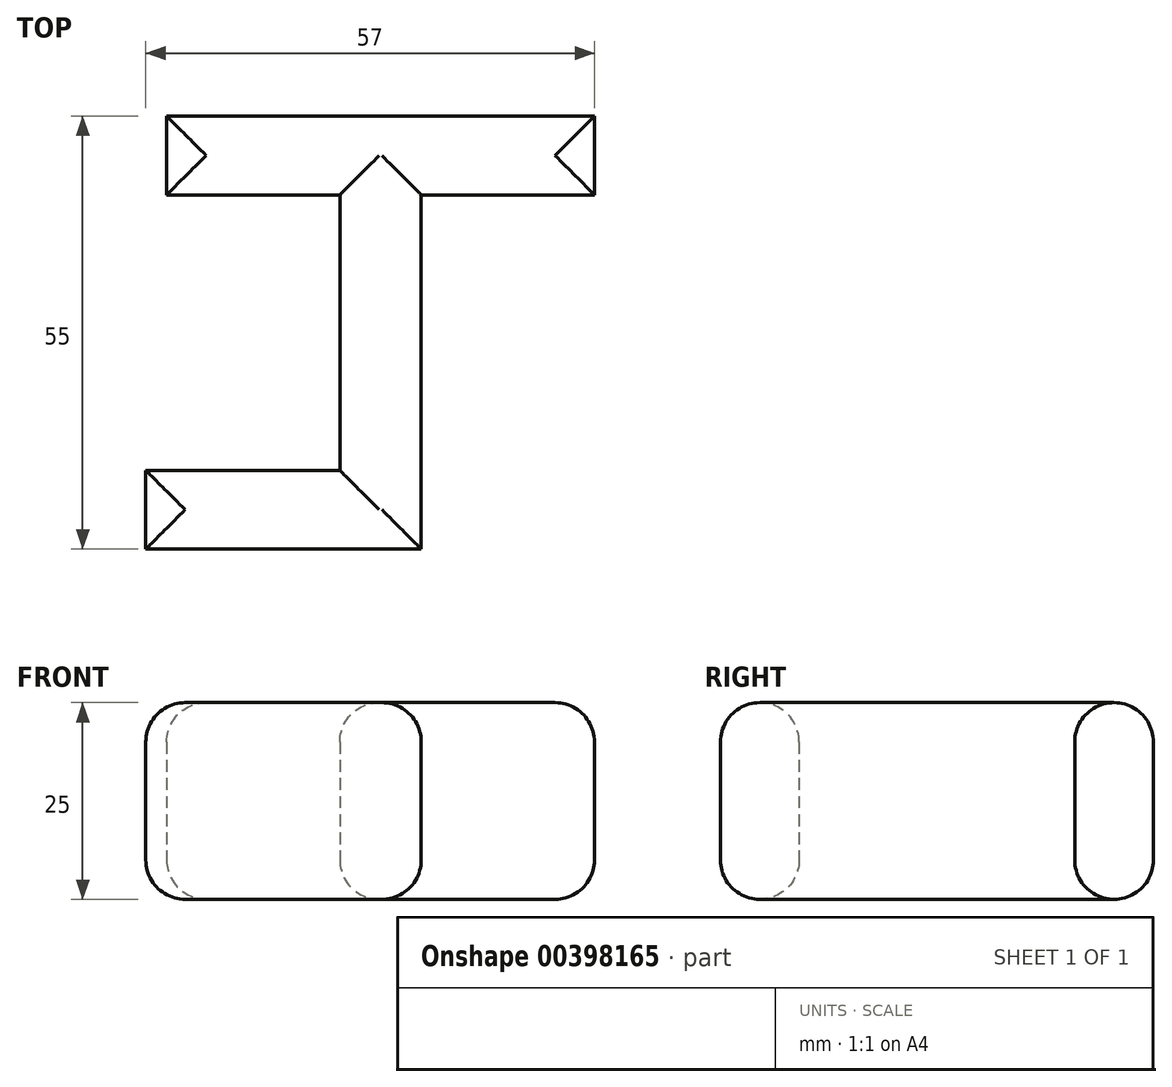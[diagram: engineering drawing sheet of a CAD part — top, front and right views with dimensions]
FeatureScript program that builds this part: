
annotation { "Feature Type Name" : "Feature", "Feature Type Description" : "" }
export const myFeature = defineFeature(function(context is Context, id is Id, definition is map)
    precondition{}
    {
        {
            var Q0;
            Q0=qCreatedBy(makeId("Top.planeOp"),FACE);
            var sketch = newSketch(context, id + "F0", { "sketchPlane" : qUnion([Q0])});
            skLineSegment(sketch, "E0", {"start": v(0, 0) * mm, "end": v(0, 45) * mm});
            skLineSegment(sketch, "E1", {"start": v(0, 0) * mm, "end": v(-35, 0) * mm});
            skLineSegment(sketch, "E2", {"start": v(-35, 0) * mm, "end": v(-35, 10) * mm});
            skLineSegment(sketch, "E3", {"start": v(-35, 10) * mm, "end": v(-10.34, 10) * mm});
            skLineSegment(sketch, "E4", {"start": v(-10.34, 10) * mm, "end": v(-10.34, 45) * mm});
            skLineSegment(sketch, "E5", {"start": v(-10.34, 45) * mm, "end": v(-32.34, 45) * mm});
            skLineSegment(sketch, "E6", {"start": v(-32.34, 45) * mm, "end": v(-32.34, 55) * mm});
            skLineSegment(sketch, "E7", {"start": v(0, 45) * mm, "end": v(22, 45) * mm});
            skLineSegment(sketch, "E8", {"start": v(22, 45) * mm, "end": v(22, 55) * mm});
            skLineSegment(sketch, "E9", {"start": v(-32.34, 55) * mm, "end": v(22, 55) * mm});
            skSolve(sketch);
        }
        {
            var Q0;
            Q0 = qSketchRegion(id + "F0", true);
            extrude(context, id + "F1", {"entities" : qUnion([Q0]), "depth" : 25 * mm});
        }
        {
            var Q0;
            Q0=makeQuery(id+"F1.opExtrude","CAP_EDGE",EDGE,{"disambiguationData":[OSD([sQuery(id+"F0.wireOp",EDGE,"E9")])],"isStart":true});
            var Q1;
            Q1=makeQuery(id+"F1.opExtrude","CAP_EDGE",EDGE,{"disambiguationData":[OSD([sQuery(id+"F0.wireOp",EDGE,"E6")])],"isStart":true});
            var Q2;
            Q2=makeQuery(id+"F1.opExtrude","CAP_EDGE",EDGE,{"disambiguationData":[OSD([sQuery(id+"F0.wireOp",EDGE,"E4")])],"isStart":true});
            var Q3;
            Q3=makeQuery(id+"F1.opExtrude","CAP_EDGE",EDGE,{"disambiguationData":[OSD([sQuery(id+"F0.wireOp",EDGE,"E5")])],"isStart":true});
            var Q4;
            Q4=makeQuery(id+"F1.opExtrude","CAP_EDGE",EDGE,{"disambiguationData":[OSD([sQuery(id+"F0.wireOp",EDGE,"E7")])],"isStart":true});
            var Q5;
            Q5=makeQuery(id+"F1.opExtrude","CAP_EDGE",EDGE,{"disambiguationData":[OSD([sQuery(id+"F0.wireOp",EDGE,"E8")])],"isStart":true});
            var Q6;
            Q6=makeQuery(id+"F1.opExtrude","CAP_EDGE",EDGE,{"disambiguationData":[OSD([sQuery(id+"F0.wireOp",EDGE,"E0")])],"isStart":true});
            var Q7;
            Q7=makeQuery(id+"F1.opExtrude","CAP_EDGE",EDGE,{"disambiguationData":[OSD([sQuery(id+"F0.wireOp",EDGE,"E1")])],"isStart":true});
            var Q8;
            Q8=makeQuery(id+"F1.opExtrude","CAP_EDGE",EDGE,{"disambiguationData":[OSD([sQuery(id+"F0.wireOp",EDGE,"E3")])],"isStart":true});
            var Q9;
            Q9=makeQuery(id+"F1.opExtrude","CAP_EDGE",EDGE,{"disambiguationData":[OSD([sQuery(id+"F0.wireOp",EDGE,"E2")])],"isStart":true});
            var Q10;
            Q10=makeQuery(id+"F1.opExtrude","CAP_EDGE",EDGE,{"disambiguationData":[OSD([sQuery(id+"F0.wireOp",EDGE,"E9")])],"isStart":false});
            var Q11;
            Q11=makeQuery(id+"F1.opExtrude","CAP_EDGE",EDGE,{"disambiguationData":[OSD([sQuery(id+"F0.wireOp",EDGE,"E7")])],"isStart":false});
            var Q12;
            Q12=makeQuery(id+"F1.opExtrude","CAP_EDGE",EDGE,{"disambiguationData":[OSD([sQuery(id+"F0.wireOp",EDGE,"E5")])],"isStart":false});
            var Q13;
            Q13=makeQuery(id+"F1.opExtrude","CAP_EDGE",EDGE,{"disambiguationData":[OSD([sQuery(id+"F0.wireOp",EDGE,"E6")])],"isStart":false});
            var Q14;
            Q14=makeQuery(id+"F1.opExtrude","CAP_EDGE",EDGE,{"disambiguationData":[OSD([sQuery(id+"F0.wireOp",EDGE,"E8")])],"isStart":false});
            var Q15;
            Q15=makeQuery(id+"F1.opExtrude","CAP_EDGE",EDGE,{"disambiguationData":[OSD([sQuery(id+"F0.wireOp",EDGE,"E4")])],"isStart":false});
            var Q16;
            Q16=makeQuery(id+"F1.opExtrude","CAP_FACE",FACE,{"disambiguationData":[OSD([sQuery(id+"F0.wireOp",EDGE,"E0"),sQuery(id+"F0.wireOp",EDGE,"E1"),sQuery(id+"F0.wireOp",EDGE,"E2"),sQuery(id+"F0.wireOp",EDGE,"E3"),sQuery(id+"F0.wireOp",EDGE,"E4"),sQuery(id+"F0.wireOp",EDGE,"E5"),sQuery(id+"F0.wireOp",EDGE,"E6"),sQuery(id+"F0.wireOp",EDGE,"E7"),sQuery(id+"F0.wireOp",EDGE,"E8"),sQuery(id+"F0.wireOp",EDGE,"E9")])],"isStart":false});
            fillet(context, id + "F2", {"entities" : qUnion([Q0, Q1, Q2, Q3, Q4, Q5, Q6, Q7, Q8, Q9, Q10, Q11, Q12, Q13, Q14, Q15, Q16]), "radius" : 5 * mm, "tangentPropagation" : true, "allowEdgeOverflow" : false});
        }
    });
